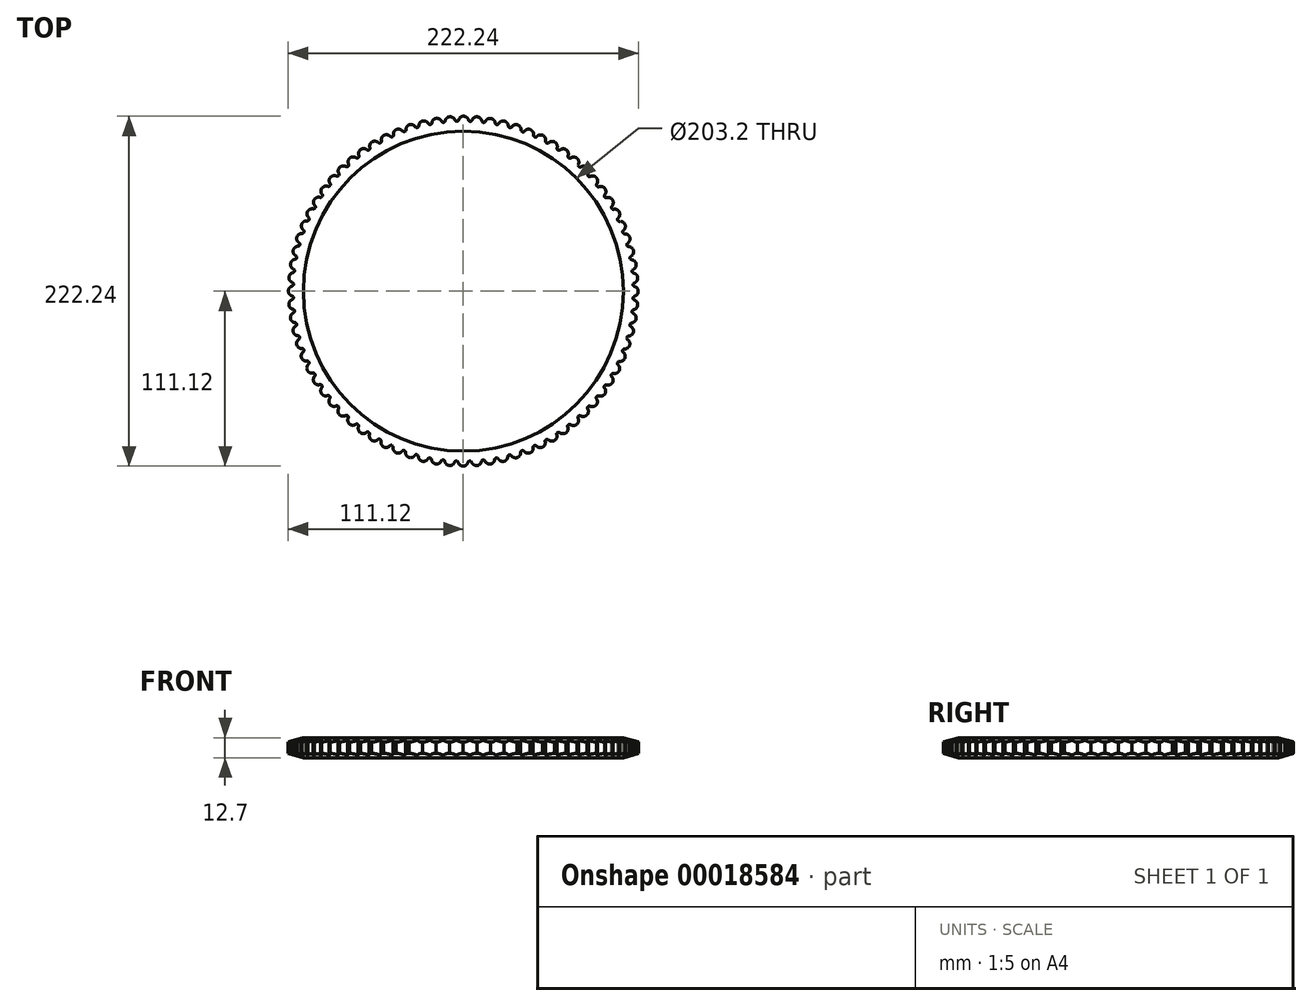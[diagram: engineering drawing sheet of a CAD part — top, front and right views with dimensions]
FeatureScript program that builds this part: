
annotation { "Feature Type Name" : "Feature", "Feature Type Description" : "" }
export const myFeature = defineFeature(function(context is Context, id is Id, definition is map)
    precondition{}
    {
        {
            var Q0;
            Q0=qCreatedBy(makeId("Top.planeOp"),FACE);
            var sketch = newSketch(context, id + "F0", { "sketchPlane" : qUnion([Q0])});
            skCircle(sketch, "E0", {"center": v(0, 0) * mm, "radius": 101.6 * mm});
            skCircle(sketch, "E1", {"center": v(0, 0) * mm, "radius": 111.13 * mm});
            skSolve(sketch);
        }
        {
            var Q0;
            Q0 = qSketchRegion(id + "F0", true);
            extrude(context, id + "F1", {"entities" : qUnion([Q0]), "depth" : 12.7 * mm});
        }
        {
            var Q0;
            Q0=makeQuery(id+"F1.opExtrude","CAP_FACE",FACE,{"disambiguationData":[OSD([sQuery(id+"F0.wireOp",EDGE,"E0"),sQuery(id+"F0.wireOp",EDGE,"E1")])],"isStart":false});
            var sketch = newSketch(context, id + "F2", { "sketchPlane" : qUnion([Q0])});
            skLineSegment(sketch, "E2", {"start": v(0, 0) * mm, "end": v(0, 111.13) * mm, "construction": true});
            skArc(sketch, "E3", {"start": v(3.3, 108.7) * mm, "mid": v(2.05, 110.45) * mm, "end": v(0, 111.13) * mm});
            skCircle(sketch, "E4", {"center": v(0, 0) * mm, "radius": 107.95 * mm, "construction": true});
            skArc(sketch, "E5", {"start": v(8.83, 110.77) * mm, "mid": v(6.85, 110.27) * mm, "end": v(5.59, 108.66) * mm});
            skArc(sketch, "E6", {"start": v(3.3, 108.7) * mm, "mid": v(4.43, 107.86) * mm, "end": v(5.59, 108.66) * mm});
            skLineSegment(sketch, "E7", {"start": v(8.58, 107.6) * mm, "end": v(8.83, 110.77) * mm, "construction": true});
            skArc(sketch, "E8.1.0", {"start": v(-5.24, 108.63) * mm, "mid": v(-6.62, 110.27) * mm, "end": v(-8.72, 110.78) * mm});
            skArc(sketch, "E8.1.1", {"start": v(0.12, 111.12) * mm, "mid": v(-1.82, 110.47) * mm, "end": v(-2.96, 108.77) * mm});
            skArc(sketch, "E8.1.2", {"start": v(-5.24, 108.63) * mm, "mid": v(-4.05, 107.87) * mm, "end": v(-2.96, 108.77) * mm});
            skArc(sketch, "E8.2.0", {"start": v(-13.74, 107.88) * mm, "mid": v(-15.26, 109.41) * mm, "end": v(-17.38, 109.76) * mm});
            skArc(sketch, "E8.2.1", {"start": v(-8.6, 110.8) * mm, "mid": v(-10.48, 109.98) * mm, "end": v(-11.48, 108.2) * mm});
            skArc(sketch, "E8.2.2", {"start": v(-13.74, 107.88) * mm, "mid": v(-12.5, 107.22) * mm, "end": v(-11.48, 108.2) * mm});
            skArc(sketch, "E8.3.0", {"start": v(-22.16, 106.47) * mm, "mid": v(-23.8, 107.88) * mm, "end": v(-25.94, 108.05) * mm});
            skArc(sketch, "E8.3.1", {"start": v(-17.27, 109.77) * mm, "mid": v(-19.08, 108.82) * mm, "end": v(-19.93, 106.97) * mm});
            skArc(sketch, "E8.3.2", {"start": v(-22.16, 106.47) * mm, "mid": v(-20.87, 105.91) * mm, "end": v(-19.93, 106.97) * mm});
            skArc(sketch, "E8.4.0", {"start": v(-30.45, 104.4) * mm, "mid": v(-32.18, 105.68) * mm, "end": v(-34.34, 105.69) * mm});
            skArc(sketch, "E8.4.1", {"start": v(-25.83, 108.08) * mm, "mid": v(-27.56, 107) * mm, "end": v(-28.26, 105.07) * mm});
            skArc(sketch, "E8.4.2", {"start": v(-30.45, 104.4) * mm, "mid": v(-29.12, 103.95) * mm, "end": v(-28.26, 105.07) * mm});
            skArc(sketch, "E8.5.0", {"start": v(-38.55, 101.7) * mm, "mid": v(-40.38, 102.83) * mm, "end": v(-42.53, 102.67) * mm});
            skArc(sketch, "E8.5.1", {"start": v(-34.23, 105.72) * mm, "mid": v(-35.87, 104.5) * mm, "end": v(-36.42, 102.53) * mm});
            skArc(sketch, "E8.5.2", {"start": v(-38.55, 101.7) * mm, "mid": v(-37.18, 101.34) * mm, "end": v(-36.42, 102.53) * mm});
            skArc(sketch, "E8.6.0", {"start": v(-46.4, 98.35) * mm, "mid": v(-48.32, 99.35) * mm, "end": v(-50.45, 99.01) * mm});
            skArc(sketch, "E8.6.1", {"start": v(-42.42, 102.71) * mm, "mid": v(-43.96, 101.36) * mm, "end": v(-44.35, 99.36) * mm});
            skArc(sketch, "E8.6.2", {"start": v(-46.4, 98.35) * mm, "mid": v(-45.02, 98.12) * mm, "end": v(-44.35, 99.36) * mm});
            skArc(sketch, "E8.7.0", {"start": v(-53.98, 94.4) * mm, "mid": v(-55.97, 95.25) * mm, "end": v(-58.06, 94.75) * mm});
            skArc(sketch, "E8.7.1", {"start": v(-50.35, 99.07) * mm, "mid": v(-51.77, 97.6) * mm, "end": v(-52.01, 95.57) * mm});
            skArc(sketch, "E8.7.2", {"start": v(-53.98, 94.4) * mm, "mid": v(-52.58, 94.28) * mm, "end": v(-52.01, 95.57) * mm});
            skArc(sketch, "E8.8.0", {"start": v(-61.22, 89.88) * mm, "mid": v(-63.27, 90.56) * mm, "end": v(-65.32, 89.9) * mm});
            skArc(sketch, "E8.8.1", {"start": v(-57.96, 94.81) * mm, "mid": v(-59.27, 93.24) * mm, "end": v(-59.35, 91.2) * mm});
            skArc(sketch, "E8.8.2", {"start": v(-61.22, 89.88) * mm, "mid": v(-59.81, 89.86) * mm, "end": v(-59.35, 91.2) * mm});
            skArc(sketch, "E8.9.0", {"start": v(-68.09, 84.8) * mm, "mid": v(-70.18, 85.32) * mm, "end": v(-72.17, 84.5) * mm});
            skArc(sketch, "E8.9.1", {"start": v(-65.22, 89.97) * mm, "mid": v(-66.4, 88.3) * mm, "end": v(-66.32, 86.26) * mm});
            skArc(sketch, "E8.9.2", {"start": v(-68.09, 84.8) * mm, "mid": v(-66.68, 84.9) * mm, "end": v(-66.32, 86.26) * mm});
            skArc(sketch, "E8.10.0", {"start": v(-74.53, 79.2) * mm, "mid": v(-76.65, 79.55) * mm, "end": v(-78.58, 78.58) * mm});
            skArc(sketch, "E8.10.1", {"start": v(-72.08, 84.58) * mm, "mid": v(-73.13, 82.82) * mm, "end": v(-72.89, 80.79) * mm});
            skArc(sketch, "E8.10.2", {"start": v(-74.53, 79.2) * mm, "mid": v(-73.13, 79.4) * mm, "end": v(-72.89, 80.79) * mm});
            skArc(sketch, "E8.11.0", {"start": v(-80.51, 73.1) * mm, "mid": v(-82.66, 73.3) * mm, "end": v(-84.5, 72.17) * mm});
            skArc(sketch, "E8.11.1", {"start": v(-78.5, 78.66) * mm, "mid": v(-79.4, 76.83) * mm, "end": v(-79, 74.82) * mm});
            skArc(sketch, "E8.11.2", {"start": v(-80.51, 73.1) * mm, "mid": v(-79.14, 73.42) * mm, "end": v(-79, 74.82) * mm});
            skArc(sketch, "E8.12.0", {"start": v(-86, 66.57) * mm, "mid": v(-88.16, 66.58) * mm, "end": v(-89.9, 65.32) * mm});
            skArc(sketch, "E8.12.1", {"start": v(-84.42, 72.26) * mm, "mid": v(-85.18, 70.36) * mm, "end": v(-84.63, 68.4) * mm});
            skArc(sketch, "E8.12.2", {"start": v(-86, 66.57) * mm, "mid": v(-84.66, 66.98) * mm, "end": v(-84.63, 68.4) * mm});
            skArc(sketch, "E8.13.0", {"start": v(-90.96, 59.61) * mm, "mid": v(-93.1, 59.46) * mm, "end": v(-94.75, 58.06) * mm});
            skArc(sketch, "E8.13.1", {"start": v(-89.83, 65.41) * mm, "mid": v(-90.44, 63.46) * mm, "end": v(-89.73, 61.54) * mm});
            skArc(sketch, "E8.13.2", {"start": v(-90.96, 59.61) * mm, "mid": v(-89.65, 60.13) * mm, "end": v(-89.73, 61.54) * mm});
            skArc(sketch, "E8.14.0", {"start": v(-95.36, 52.3) * mm, "mid": v(-97.49, 51.97) * mm, "end": v(-99.01, 50.45) * mm});
            skArc(sketch, "E8.14.1", {"start": v(-94.69, 58.16) * mm, "mid": v(-95.14, 56.17) * mm, "end": v(-94.28, 54.31) * mm});
            skArc(sketch, "E8.14.2", {"start": v(-95.36, 52.3) * mm, "mid": v(-94.1, 52.92) * mm, "end": v(-94.28, 54.31) * mm});
            skArc(sketch, "E8.15.0", {"start": v(-99.16, 44.65) * mm, "mid": v(-101.26, 44.16) * mm, "end": v(-102.67, 42.53) * mm});
            skArc(sketch, "E8.15.1", {"start": v(-98.96, 50.55) * mm, "mid": v(-99.25, 48.53) * mm, "end": v(-98.25, 46.75) * mm});
            skArc(sketch, "E8.15.2", {"start": v(-99.16, 44.65) * mm, "mid": v(-97.95, 45.37) * mm, "end": v(-98.25, 46.75) * mm});
            skArc(sketch, "E8.16.0", {"start": v(-102.36, 36.73) * mm, "mid": v(-104.42, 36.08) * mm, "end": v(-105.69, 34.34) * mm});
            skArc(sketch, "E8.16.1", {"start": v(-102.62, 42.63) * mm, "mid": v(-102.76, 40.6) * mm, "end": v(-101.62, 38.9) * mm});
            skArc(sketch, "E8.16.2", {"start": v(-102.36, 36.73) * mm, "mid": v(-101.21, 37.54) * mm, "end": v(-101.62, 38.9) * mm});
            skArc(sketch, "E8.17.0", {"start": v(-104.93, 28.59) * mm, "mid": v(-106.92, 27.78) * mm, "end": v(-108.05, 25.94) * mm});
            skArc(sketch, "E8.17.1", {"start": v(-105.65, 34.45) * mm, "mid": v(-105.62, 32.4) * mm, "end": v(-104.36, 30.8) * mm});
            skArc(sketch, "E8.17.2", {"start": v(-104.93, 28.59) * mm, "mid": v(-103.84, 29.49) * mm, "end": v(-104.36, 30.8) * mm});
            skArc(sketch, "E8.18.0", {"start": v(-106.85, 20.27) * mm, "mid": v(-108.77, 19.3) * mm, "end": v(-109.76, 17.38) * mm});
            skArc(sketch, "E8.18.1", {"start": v(-108.03, 26.05) * mm, "mid": v(-107.84, 24.02) * mm, "end": v(-106.45, 22.52) * mm});
            skArc(sketch, "E8.18.2", {"start": v(-106.85, 20.27) * mm, "mid": v(-105.84, 21.25) * mm, "end": v(-106.45, 22.52) * mm});
            skArc(sketch, "E8.19.0", {"start": v(-108.1, 11.82) * mm, "mid": v(-109.95, 10.7) * mm, "end": v(-110.78, 8.72) * mm});
            skArc(sketch, "E8.19.1", {"start": v(-109.74, 17.5) * mm, "mid": v(-109.4, 15.48) * mm, "end": v(-107.9, 14.1) * mm});
            skArc(sketch, "E8.19.2", {"start": v(-108.1, 11.82) * mm, "mid": v(-107.18, 12.88) * mm, "end": v(-107.9, 14.1) * mm});
            skArc(sketch, "E8.20.0", {"start": v(-108.7, 3.3) * mm, "mid": v(-110.45, 2.05) * mm, "end": v(-111.13, 0) * mm});
            skArc(sketch, "E8.20.1", {"start": v(-110.77, 8.83) * mm, "mid": v(-110.27, 6.85) * mm, "end": v(-108.66, 5.59) * mm});
            skArc(sketch, "E8.20.2", {"start": v(-108.7, 3.3) * mm, "mid": v(-107.86, 4.43) * mm, "end": v(-108.66, 5.59) * mm});
            skArc(sketch, "E8.21.0", {"start": v(-108.63, -5.24) * mm, "mid": v(-110.27, -6.62) * mm, "end": v(-110.78, -8.72) * mm});
            skArc(sketch, "E8.21.1", {"start": v(-111.12, 0.12) * mm, "mid": v(-110.47, -1.82) * mm, "end": v(-108.77, -2.96) * mm});
            skArc(sketch, "E8.21.2", {"start": v(-108.63, -5.24) * mm, "mid": v(-107.87, -4.05) * mm, "end": v(-108.77, -2.96) * mm});
            skArc(sketch, "E8.22.0", {"start": v(-107.88, -13.74) * mm, "mid": v(-109.41, -15.26) * mm, "end": v(-109.76, -17.38) * mm});
            skArc(sketch, "E8.22.1", {"start": v(-110.8, -8.6) * mm, "mid": v(-109.98, -10.48) * mm, "end": v(-108.2, -11.48) * mm});
            skArc(sketch, "E8.22.2", {"start": v(-107.88, -13.74) * mm, "mid": v(-107.22, -12.5) * mm, "end": v(-108.2, -11.48) * mm});
            skArc(sketch, "E8.23.0", {"start": v(-106.47, -22.16) * mm, "mid": v(-107.88, -23.8) * mm, "end": v(-108.05, -25.94) * mm});
            skArc(sketch, "E8.23.1", {"start": v(-109.77, -17.27) * mm, "mid": v(-108.82, -19.08) * mm, "end": v(-106.97, -19.93) * mm});
            skArc(sketch, "E8.23.2", {"start": v(-106.47, -22.16) * mm, "mid": v(-105.91, -20.87) * mm, "end": v(-106.97, -19.93) * mm});
            skArc(sketch, "E8.24.0", {"start": v(-104.4, -30.45) * mm, "mid": v(-105.68, -32.18) * mm, "end": v(-105.69, -34.34) * mm});
            skArc(sketch, "E8.24.1", {"start": v(-108.08, -25.83) * mm, "mid": v(-107, -27.56) * mm, "end": v(-105.07, -28.26) * mm});
            skArc(sketch, "E8.24.2", {"start": v(-104.4, -30.45) * mm, "mid": v(-103.95, -29.12) * mm, "end": v(-105.07, -28.26) * mm});
            skArc(sketch, "E8.25.0", {"start": v(-101.7, -38.55) * mm, "mid": v(-102.83, -40.38) * mm, "end": v(-102.67, -42.53) * mm});
            skArc(sketch, "E8.25.1", {"start": v(-105.72, -34.23) * mm, "mid": v(-104.5, -35.87) * mm, "end": v(-102.53, -36.42) * mm});
            skArc(sketch, "E8.25.2", {"start": v(-101.7, -38.55) * mm, "mid": v(-101.34, -37.18) * mm, "end": v(-102.53, -36.42) * mm});
            skArc(sketch, "E8.26.0", {"start": v(-98.35, -46.4) * mm, "mid": v(-99.35, -48.32) * mm, "end": v(-99.01, -50.45) * mm});
            skArc(sketch, "E8.26.1", {"start": v(-102.71, -42.42) * mm, "mid": v(-101.36, -43.96) * mm, "end": v(-99.36, -44.35) * mm});
            skArc(sketch, "E8.26.2", {"start": v(-98.35, -46.4) * mm, "mid": v(-98.12, -45.02) * mm, "end": v(-99.36, -44.35) * mm});
            skArc(sketch, "E8.27.0", {"start": v(-94.4, -53.98) * mm, "mid": v(-95.25, -55.97) * mm, "end": v(-94.75, -58.06) * mm});
            skArc(sketch, "E8.27.1", {"start": v(-99.07, -50.35) * mm, "mid": v(-97.6, -51.77) * mm, "end": v(-95.57, -52.01) * mm});
            skArc(sketch, "E8.27.2", {"start": v(-94.4, -53.98) * mm, "mid": v(-94.28, -52.58) * mm, "end": v(-95.57, -52.01) * mm});
            skArc(sketch, "E8.28.0", {"start": v(-89.88, -61.22) * mm, "mid": v(-90.56, -63.27) * mm, "end": v(-89.9, -65.32) * mm});
            skArc(sketch, "E8.28.1", {"start": v(-94.81, -57.96) * mm, "mid": v(-93.24, -59.27) * mm, "end": v(-91.2, -59.35) * mm});
            skArc(sketch, "E8.28.2", {"start": v(-89.88, -61.22) * mm, "mid": v(-89.86, -59.81) * mm, "end": v(-91.2, -59.35) * mm});
            skArc(sketch, "E8.29.0", {"start": v(-84.8, -68.09) * mm, "mid": v(-85.32, -70.18) * mm, "end": v(-84.5, -72.17) * mm});
            skArc(sketch, "E8.29.1", {"start": v(-89.97, -65.22) * mm, "mid": v(-88.3, -66.4) * mm, "end": v(-86.26, -66.32) * mm});
            skArc(sketch, "E8.29.2", {"start": v(-84.8, -68.09) * mm, "mid": v(-84.9, -66.68) * mm, "end": v(-86.26, -66.32) * mm});
            skArc(sketch, "E8.30.0", {"start": v(-79.2, -74.53) * mm, "mid": v(-79.55, -76.65) * mm, "end": v(-78.58, -78.58) * mm});
            skArc(sketch, "E8.30.1", {"start": v(-84.58, -72.08) * mm, "mid": v(-82.82, -73.13) * mm, "end": v(-80.79, -72.89) * mm});
            skArc(sketch, "E8.30.2", {"start": v(-79.2, -74.53) * mm, "mid": v(-79.4, -73.13) * mm, "end": v(-80.79, -72.89) * mm});
            skArc(sketch, "E8.31.0", {"start": v(-73.1, -80.51) * mm, "mid": v(-73.3, -82.66) * mm, "end": v(-72.17, -84.5) * mm});
            skArc(sketch, "E8.31.1", {"start": v(-78.66, -78.5) * mm, "mid": v(-76.83, -79.4) * mm, "end": v(-74.82, -79) * mm});
            skArc(sketch, "E8.31.2", {"start": v(-73.1, -80.51) * mm, "mid": v(-73.42, -79.14) * mm, "end": v(-74.82, -79) * mm});
            skArc(sketch, "E8.32.0", {"start": v(-66.57, -86) * mm, "mid": v(-66.58, -88.16) * mm, "end": v(-65.32, -89.9) * mm});
            skArc(sketch, "E8.32.1", {"start": v(-72.26, -84.42) * mm, "mid": v(-70.36, -85.18) * mm, "end": v(-68.4, -84.63) * mm});
            skArc(sketch, "E8.32.2", {"start": v(-66.57, -86) * mm, "mid": v(-66.98, -84.66) * mm, "end": v(-68.4, -84.63) * mm});
            skArc(sketch, "E8.33.0", {"start": v(-59.61, -90.96) * mm, "mid": v(-59.46, -93.1) * mm, "end": v(-58.06, -94.75) * mm});
            skArc(sketch, "E8.33.1", {"start": v(-65.41, -89.83) * mm, "mid": v(-63.46, -90.44) * mm, "end": v(-61.54, -89.73) * mm});
            skArc(sketch, "E8.33.2", {"start": v(-59.61, -90.96) * mm, "mid": v(-60.13, -89.65) * mm, "end": v(-61.54, -89.73) * mm});
            skArc(sketch, "E8.34.0", {"start": v(-52.3, -95.36) * mm, "mid": v(-51.97, -97.49) * mm, "end": v(-50.45, -99.01) * mm});
            skArc(sketch, "E8.34.1", {"start": v(-58.16, -94.69) * mm, "mid": v(-56.17, -95.14) * mm, "end": v(-54.31, -94.28) * mm});
            skArc(sketch, "E8.34.2", {"start": v(-52.3, -95.36) * mm, "mid": v(-52.92, -94.1) * mm, "end": v(-54.31, -94.28) * mm});
            skArc(sketch, "E8.35.0", {"start": v(-44.65, -99.16) * mm, "mid": v(-44.16, -101.26) * mm, "end": v(-42.53, -102.67) * mm});
            skArc(sketch, "E8.35.1", {"start": v(-50.55, -98.96) * mm, "mid": v(-48.53, -99.25) * mm, "end": v(-46.75, -98.25) * mm});
            skArc(sketch, "E8.35.2", {"start": v(-44.65, -99.16) * mm, "mid": v(-45.37, -97.95) * mm, "end": v(-46.75, -98.25) * mm});
            skArc(sketch, "E8.36.0", {"start": v(-36.73, -102.36) * mm, "mid": v(-36.08, -104.42) * mm, "end": v(-34.34, -105.69) * mm});
            skArc(sketch, "E8.36.1", {"start": v(-42.63, -102.62) * mm, "mid": v(-40.6, -102.76) * mm, "end": v(-38.9, -101.62) * mm});
            skArc(sketch, "E8.36.2", {"start": v(-36.73, -102.36) * mm, "mid": v(-37.54, -101.21) * mm, "end": v(-38.9, -101.62) * mm});
            skArc(sketch, "E8.37.0", {"start": v(-28.59, -104.93) * mm, "mid": v(-27.78, -106.92) * mm, "end": v(-25.94, -108.05) * mm});
            skArc(sketch, "E8.37.1", {"start": v(-34.45, -105.65) * mm, "mid": v(-32.4, -105.62) * mm, "end": v(-30.8, -104.36) * mm});
            skArc(sketch, "E8.37.2", {"start": v(-28.59, -104.93) * mm, "mid": v(-29.49, -103.84) * mm, "end": v(-30.8, -104.36) * mm});
            skArc(sketch, "E8.38.0", {"start": v(-20.27, -106.85) * mm, "mid": v(-19.3, -108.77) * mm, "end": v(-17.38, -109.76) * mm});
            skArc(sketch, "E8.38.1", {"start": v(-26.05, -108.03) * mm, "mid": v(-24.02, -107.84) * mm, "end": v(-22.52, -106.45) * mm});
            skArc(sketch, "E8.38.2", {"start": v(-20.27, -106.85) * mm, "mid": v(-21.25, -105.84) * mm, "end": v(-22.52, -106.45) * mm});
            skArc(sketch, "E8.39.0", {"start": v(-11.82, -108.1) * mm, "mid": v(-10.7, -109.95) * mm, "end": v(-8.72, -110.78) * mm});
            skArc(sketch, "E8.39.1", {"start": v(-17.5, -109.74) * mm, "mid": v(-15.48, -109.4) * mm, "end": v(-14.1, -107.9) * mm});
            skArc(sketch, "E8.39.2", {"start": v(-11.82, -108.1) * mm, "mid": v(-12.88, -107.18) * mm, "end": v(-14.1, -107.9) * mm});
            skArc(sketch, "E8.40.0", {"start": v(-3.3, -108.7) * mm, "mid": v(-2.05, -110.45) * mm, "end": v(0, -111.13) * mm});
            skArc(sketch, "E8.40.1", {"start": v(-8.83, -110.77) * mm, "mid": v(-6.85, -110.27) * mm, "end": v(-5.59, -108.66) * mm});
            skArc(sketch, "E8.40.2", {"start": v(-3.3, -108.7) * mm, "mid": v(-4.43, -107.86) * mm, "end": v(-5.59, -108.66) * mm});
            skArc(sketch, "E8.41.0", {"start": v(5.24, -108.63) * mm, "mid": v(6.62, -110.27) * mm, "end": v(8.72, -110.78) * mm});
            skArc(sketch, "E8.41.1", {"start": v(-0.12, -111.12) * mm, "mid": v(1.82, -110.47) * mm, "end": v(2.96, -108.77) * mm});
            skArc(sketch, "E8.41.2", {"start": v(5.24, -108.63) * mm, "mid": v(4.05, -107.87) * mm, "end": v(2.96, -108.77) * mm});
            skArc(sketch, "E8.42.0", {"start": v(13.74, -107.88) * mm, "mid": v(15.26, -109.41) * mm, "end": v(17.38, -109.76) * mm});
            skArc(sketch, "E8.42.1", {"start": v(8.6, -110.8) * mm, "mid": v(10.48, -109.98) * mm, "end": v(11.48, -108.2) * mm});
            skArc(sketch, "E8.42.2", {"start": v(13.74, -107.88) * mm, "mid": v(12.5, -107.22) * mm, "end": v(11.48, -108.2) * mm});
            skArc(sketch, "E8.43.0", {"start": v(22.16, -106.47) * mm, "mid": v(23.8, -107.88) * mm, "end": v(25.94, -108.05) * mm});
            skArc(sketch, "E8.43.1", {"start": v(17.27, -109.77) * mm, "mid": v(19.08, -108.82) * mm, "end": v(19.93, -106.97) * mm});
            skArc(sketch, "E8.43.2", {"start": v(22.16, -106.47) * mm, "mid": v(20.87, -105.91) * mm, "end": v(19.93, -106.97) * mm});
            skArc(sketch, "E8.44.0", {"start": v(30.45, -104.4) * mm, "mid": v(32.18, -105.68) * mm, "end": v(34.34, -105.69) * mm});
            skArc(sketch, "E8.44.1", {"start": v(25.83, -108.08) * mm, "mid": v(27.56, -107) * mm, "end": v(28.26, -105.07) * mm});
            skArc(sketch, "E8.44.2", {"start": v(30.45, -104.4) * mm, "mid": v(29.12, -103.95) * mm, "end": v(28.26, -105.07) * mm});
            skArc(sketch, "E8.45.0", {"start": v(38.55, -101.7) * mm, "mid": v(40.38, -102.83) * mm, "end": v(42.53, -102.67) * mm});
            skArc(sketch, "E8.45.1", {"start": v(34.23, -105.72) * mm, "mid": v(35.87, -104.5) * mm, "end": v(36.42, -102.53) * mm});
            skArc(sketch, "E8.45.2", {"start": v(38.55, -101.7) * mm, "mid": v(37.18, -101.34) * mm, "end": v(36.42, -102.53) * mm});
            skArc(sketch, "E8.46.0", {"start": v(46.4, -98.35) * mm, "mid": v(48.32, -99.35) * mm, "end": v(50.45, -99.01) * mm});
            skArc(sketch, "E8.46.1", {"start": v(42.42, -102.71) * mm, "mid": v(43.96, -101.36) * mm, "end": v(44.35, -99.36) * mm});
            skArc(sketch, "E8.46.2", {"start": v(46.4, -98.35) * mm, "mid": v(45.02, -98.12) * mm, "end": v(44.35, -99.36) * mm});
            skArc(sketch, "E8.47.0", {"start": v(53.98, -94.4) * mm, "mid": v(55.97, -95.25) * mm, "end": v(58.06, -94.75) * mm});
            skArc(sketch, "E8.47.1", {"start": v(50.35, -99.07) * mm, "mid": v(51.77, -97.6) * mm, "end": v(52.01, -95.57) * mm});
            skArc(sketch, "E8.47.2", {"start": v(53.98, -94.4) * mm, "mid": v(52.58, -94.28) * mm, "end": v(52.01, -95.57) * mm});
            skArc(sketch, "E8.48.0", {"start": v(61.22, -89.88) * mm, "mid": v(63.27, -90.56) * mm, "end": v(65.32, -89.9) * mm});
            skArc(sketch, "E8.48.1", {"start": v(57.96, -94.81) * mm, "mid": v(59.27, -93.24) * mm, "end": v(59.35, -91.2) * mm});
            skArc(sketch, "E8.48.2", {"start": v(61.22, -89.88) * mm, "mid": v(59.81, -89.86) * mm, "end": v(59.35, -91.2) * mm});
            skArc(sketch, "E8.49.0", {"start": v(68.09, -84.8) * mm, "mid": v(70.18, -85.32) * mm, "end": v(72.17, -84.5) * mm});
            skArc(sketch, "E8.49.1", {"start": v(65.22, -89.97) * mm, "mid": v(66.4, -88.3) * mm, "end": v(66.32, -86.26) * mm});
            skArc(sketch, "E8.49.2", {"start": v(68.09, -84.8) * mm, "mid": v(66.68, -84.9) * mm, "end": v(66.32, -86.26) * mm});
            skArc(sketch, "E8.50.0", {"start": v(74.53, -79.2) * mm, "mid": v(76.65, -79.55) * mm, "end": v(78.58, -78.58) * mm});
            skArc(sketch, "E8.50.1", {"start": v(72.08, -84.58) * mm, "mid": v(73.13, -82.82) * mm, "end": v(72.89, -80.79) * mm});
            skArc(sketch, "E8.50.2", {"start": v(74.53, -79.2) * mm, "mid": v(73.13, -79.4) * mm, "end": v(72.89, -80.79) * mm});
            skArc(sketch, "E8.51.0", {"start": v(80.51, -73.1) * mm, "mid": v(82.66, -73.3) * mm, "end": v(84.5, -72.17) * mm});
            skArc(sketch, "E8.51.1", {"start": v(78.5, -78.66) * mm, "mid": v(79.4, -76.83) * mm, "end": v(79, -74.82) * mm});
            skArc(sketch, "E8.51.2", {"start": v(80.51, -73.1) * mm, "mid": v(79.14, -73.42) * mm, "end": v(79, -74.82) * mm});
            skArc(sketch, "E8.52.0", {"start": v(86, -66.57) * mm, "mid": v(88.16, -66.58) * mm, "end": v(89.9, -65.32) * mm});
            skArc(sketch, "E8.52.1", {"start": v(84.42, -72.26) * mm, "mid": v(85.18, -70.36) * mm, "end": v(84.63, -68.4) * mm});
            skArc(sketch, "E8.52.2", {"start": v(86, -66.57) * mm, "mid": v(84.66, -66.98) * mm, "end": v(84.63, -68.4) * mm});
            skArc(sketch, "E8.53.0", {"start": v(90.96, -59.61) * mm, "mid": v(93.1, -59.46) * mm, "end": v(94.75, -58.06) * mm});
            skArc(sketch, "E8.53.1", {"start": v(89.83, -65.41) * mm, "mid": v(90.44, -63.46) * mm, "end": v(89.73, -61.54) * mm});
            skArc(sketch, "E8.53.2", {"start": v(90.96, -59.61) * mm, "mid": v(89.65, -60.13) * mm, "end": v(89.73, -61.54) * mm});
            skArc(sketch, "E8.54.0", {"start": v(95.36, -52.3) * mm, "mid": v(97.49, -51.97) * mm, "end": v(99.01, -50.45) * mm});
            skArc(sketch, "E8.54.1", {"start": v(94.69, -58.16) * mm, "mid": v(95.14, -56.17) * mm, "end": v(94.28, -54.31) * mm});
            skArc(sketch, "E8.54.2", {"start": v(95.36, -52.3) * mm, "mid": v(94.1, -52.92) * mm, "end": v(94.28, -54.31) * mm});
            skArc(sketch, "E8.55.0", {"start": v(99.16, -44.65) * mm, "mid": v(101.26, -44.16) * mm, "end": v(102.67, -42.53) * mm});
            skArc(sketch, "E8.55.1", {"start": v(98.96, -50.55) * mm, "mid": v(99.25, -48.53) * mm, "end": v(98.25, -46.75) * mm});
            skArc(sketch, "E8.55.2", {"start": v(99.16, -44.65) * mm, "mid": v(97.95, -45.37) * mm, "end": v(98.25, -46.75) * mm});
            skArc(sketch, "E8.56.0", {"start": v(102.36, -36.73) * mm, "mid": v(104.42, -36.08) * mm, "end": v(105.69, -34.34) * mm});
            skArc(sketch, "E8.56.1", {"start": v(102.62, -42.63) * mm, "mid": v(102.76, -40.6) * mm, "end": v(101.62, -38.9) * mm});
            skArc(sketch, "E8.56.2", {"start": v(102.36, -36.73) * mm, "mid": v(101.21, -37.54) * mm, "end": v(101.62, -38.9) * mm});
            skArc(sketch, "E8.57.0", {"start": v(104.93, -28.59) * mm, "mid": v(106.92, -27.78) * mm, "end": v(108.05, -25.94) * mm});
            skArc(sketch, "E8.57.1", {"start": v(105.65, -34.45) * mm, "mid": v(105.62, -32.4) * mm, "end": v(104.36, -30.8) * mm});
            skArc(sketch, "E8.57.2", {"start": v(104.93, -28.59) * mm, "mid": v(103.84, -29.49) * mm, "end": v(104.36, -30.8) * mm});
            skArc(sketch, "E8.58.0", {"start": v(106.85, -20.27) * mm, "mid": v(108.77, -19.3) * mm, "end": v(109.76, -17.38) * mm});
            skArc(sketch, "E8.58.1", {"start": v(108.03, -26.05) * mm, "mid": v(107.84, -24.02) * mm, "end": v(106.45, -22.52) * mm});
            skArc(sketch, "E8.58.2", {"start": v(106.85, -20.27) * mm, "mid": v(105.84, -21.25) * mm, "end": v(106.45, -22.52) * mm});
            skArc(sketch, "E8.59.0", {"start": v(108.1, -11.82) * mm, "mid": v(109.95, -10.7) * mm, "end": v(110.78, -8.72) * mm});
            skArc(sketch, "E8.59.1", {"start": v(109.74, -17.5) * mm, "mid": v(109.4, -15.48) * mm, "end": v(107.9, -14.1) * mm});
            skArc(sketch, "E8.59.2", {"start": v(108.1, -11.82) * mm, "mid": v(107.18, -12.88) * mm, "end": v(107.9, -14.1) * mm});
            skArc(sketch, "E8.60.0", {"start": v(108.7, -3.3) * mm, "mid": v(110.45, -2.05) * mm, "end": v(111.13, 0) * mm});
            skArc(sketch, "E8.60.1", {"start": v(110.77, -8.83) * mm, "mid": v(110.27, -6.85) * mm, "end": v(108.66, -5.59) * mm});
            skArc(sketch, "E8.60.2", {"start": v(108.7, -3.3) * mm, "mid": v(107.86, -4.43) * mm, "end": v(108.66, -5.59) * mm});
            skArc(sketch, "E8.61.0", {"start": v(108.63, 5.24) * mm, "mid": v(110.27, 6.62) * mm, "end": v(110.78, 8.72) * mm});
            skArc(sketch, "E8.61.1", {"start": v(111.12, -0.12) * mm, "mid": v(110.47, 1.82) * mm, "end": v(108.77, 2.96) * mm});
            skArc(sketch, "E8.61.2", {"start": v(108.63, 5.24) * mm, "mid": v(107.87, 4.05) * mm, "end": v(108.77, 2.96) * mm});
            skArc(sketch, "E8.62.0", {"start": v(107.88, 13.74) * mm, "mid": v(109.41, 15.26) * mm, "end": v(109.76, 17.38) * mm});
            skArc(sketch, "E8.62.1", {"start": v(110.8, 8.6) * mm, "mid": v(109.98, 10.48) * mm, "end": v(108.2, 11.48) * mm});
            skArc(sketch, "E8.62.2", {"start": v(107.88, 13.74) * mm, "mid": v(107.22, 12.5) * mm, "end": v(108.2, 11.48) * mm});
            skArc(sketch, "E8.63.0", {"start": v(106.47, 22.16) * mm, "mid": v(107.88, 23.8) * mm, "end": v(108.05, 25.94) * mm});
            skArc(sketch, "E8.63.1", {"start": v(109.77, 17.27) * mm, "mid": v(108.82, 19.08) * mm, "end": v(106.97, 19.93) * mm});
            skArc(sketch, "E8.63.2", {"start": v(106.47, 22.16) * mm, "mid": v(105.91, 20.87) * mm, "end": v(106.97, 19.93) * mm});
            skArc(sketch, "E8.64.0", {"start": v(104.4, 30.45) * mm, "mid": v(105.68, 32.18) * mm, "end": v(105.69, 34.34) * mm});
            skArc(sketch, "E8.64.1", {"start": v(108.08, 25.83) * mm, "mid": v(107, 27.56) * mm, "end": v(105.07, 28.26) * mm});
            skArc(sketch, "E8.64.2", {"start": v(104.4, 30.45) * mm, "mid": v(103.95, 29.12) * mm, "end": v(105.07, 28.26) * mm});
            skArc(sketch, "E8.65.0", {"start": v(101.7, 38.55) * mm, "mid": v(102.83, 40.38) * mm, "end": v(102.67, 42.53) * mm});
            skArc(sketch, "E8.65.1", {"start": v(105.72, 34.23) * mm, "mid": v(104.5, 35.87) * mm, "end": v(102.53, 36.42) * mm});
            skArc(sketch, "E8.65.2", {"start": v(101.7, 38.55) * mm, "mid": v(101.34, 37.18) * mm, "end": v(102.53, 36.42) * mm});
            skArc(sketch, "E8.66.0", {"start": v(98.35, 46.4) * mm, "mid": v(99.35, 48.32) * mm, "end": v(99.01, 50.45) * mm});
            skArc(sketch, "E8.66.1", {"start": v(102.71, 42.42) * mm, "mid": v(101.36, 43.96) * mm, "end": v(99.36, 44.35) * mm});
            skArc(sketch, "E8.66.2", {"start": v(98.35, 46.4) * mm, "mid": v(98.12, 45.02) * mm, "end": v(99.36, 44.35) * mm});
            skArc(sketch, "E8.67.0", {"start": v(94.4, 53.98) * mm, "mid": v(95.25, 55.97) * mm, "end": v(94.75, 58.06) * mm});
            skArc(sketch, "E8.67.1", {"start": v(99.07, 50.35) * mm, "mid": v(97.6, 51.77) * mm, "end": v(95.57, 52.01) * mm});
            skArc(sketch, "E8.67.2", {"start": v(94.4, 53.98) * mm, "mid": v(94.28, 52.58) * mm, "end": v(95.57, 52.01) * mm});
            skArc(sketch, "E8.68.0", {"start": v(89.88, 61.22) * mm, "mid": v(90.56, 63.27) * mm, "end": v(89.9, 65.32) * mm});
            skArc(sketch, "E8.68.1", {"start": v(94.81, 57.96) * mm, "mid": v(93.24, 59.27) * mm, "end": v(91.2, 59.35) * mm});
            skArc(sketch, "E8.68.2", {"start": v(89.88, 61.22) * mm, "mid": v(89.86, 59.81) * mm, "end": v(91.2, 59.35) * mm});
            skArc(sketch, "E8.69.0", {"start": v(84.8, 68.09) * mm, "mid": v(85.32, 70.18) * mm, "end": v(84.5, 72.17) * mm});
            skArc(sketch, "E8.69.1", {"start": v(89.97, 65.22) * mm, "mid": v(88.3, 66.4) * mm, "end": v(86.26, 66.32) * mm});
            skArc(sketch, "E8.69.2", {"start": v(84.8, 68.09) * mm, "mid": v(84.9, 66.68) * mm, "end": v(86.26, 66.32) * mm});
            skArc(sketch, "E8.70.0", {"start": v(79.2, 74.53) * mm, "mid": v(79.55, 76.65) * mm, "end": v(78.58, 78.58) * mm});
            skArc(sketch, "E8.70.1", {"start": v(84.58, 72.08) * mm, "mid": v(82.82, 73.13) * mm, "end": v(80.79, 72.89) * mm});
            skArc(sketch, "E8.70.2", {"start": v(79.2, 74.53) * mm, "mid": v(79.4, 73.13) * mm, "end": v(80.79, 72.89) * mm});
            skArc(sketch, "E8.71.0", {"start": v(73.1, 80.51) * mm, "mid": v(73.3, 82.66) * mm, "end": v(72.17, 84.5) * mm});
            skArc(sketch, "E8.71.1", {"start": v(78.66, 78.5) * mm, "mid": v(76.83, 79.4) * mm, "end": v(74.82, 79) * mm});
            skArc(sketch, "E8.71.2", {"start": v(73.1, 80.51) * mm, "mid": v(73.42, 79.14) * mm, "end": v(74.82, 79) * mm});
            skArc(sketch, "E8.72.0", {"start": v(66.57, 86) * mm, "mid": v(66.58, 88.16) * mm, "end": v(65.32, 89.9) * mm});
            skArc(sketch, "E8.72.1", {"start": v(72.26, 84.42) * mm, "mid": v(70.36, 85.18) * mm, "end": v(68.4, 84.63) * mm});
            skArc(sketch, "E8.72.2", {"start": v(66.57, 86) * mm, "mid": v(66.98, 84.66) * mm, "end": v(68.4, 84.63) * mm});
            skArc(sketch, "E8.73.0", {"start": v(59.61, 90.96) * mm, "mid": v(59.46, 93.1) * mm, "end": v(58.06, 94.75) * mm});
            skArc(sketch, "E8.73.1", {"start": v(65.41, 89.83) * mm, "mid": v(63.46, 90.44) * mm, "end": v(61.54, 89.73) * mm});
            skArc(sketch, "E8.73.2", {"start": v(59.61, 90.96) * mm, "mid": v(60.13, 89.65) * mm, "end": v(61.54, 89.73) * mm});
            skArc(sketch, "E8.74.0", {"start": v(52.3, 95.36) * mm, "mid": v(51.97, 97.49) * mm, "end": v(50.45, 99.01) * mm});
            skArc(sketch, "E8.74.1", {"start": v(58.16, 94.69) * mm, "mid": v(56.17, 95.14) * mm, "end": v(54.31, 94.28) * mm});
            skArc(sketch, "E8.74.2", {"start": v(52.3, 95.36) * mm, "mid": v(52.92, 94.1) * mm, "end": v(54.31, 94.28) * mm});
            skArc(sketch, "E8.75.0", {"start": v(44.65, 99.16) * mm, "mid": v(44.16, 101.26) * mm, "end": v(42.53, 102.67) * mm});
            skArc(sketch, "E8.75.1", {"start": v(50.55, 98.96) * mm, "mid": v(48.53, 99.25) * mm, "end": v(46.75, 98.25) * mm});
            skArc(sketch, "E8.75.2", {"start": v(44.65, 99.16) * mm, "mid": v(45.37, 97.95) * mm, "end": v(46.75, 98.25) * mm});
            skArc(sketch, "E8.76.0", {"start": v(36.73, 102.36) * mm, "mid": v(36.08, 104.42) * mm, "end": v(34.34, 105.69) * mm});
            skArc(sketch, "E8.76.1", {"start": v(42.63, 102.62) * mm, "mid": v(40.6, 102.76) * mm, "end": v(38.9, 101.62) * mm});
            skArc(sketch, "E8.76.2", {"start": v(36.73, 102.36) * mm, "mid": v(37.54, 101.21) * mm, "end": v(38.9, 101.62) * mm});
            skArc(sketch, "E8.77.0", {"start": v(28.59, 104.93) * mm, "mid": v(27.78, 106.92) * mm, "end": v(25.94, 108.05) * mm});
            skArc(sketch, "E8.77.1", {"start": v(34.45, 105.65) * mm, "mid": v(32.4, 105.62) * mm, "end": v(30.8, 104.36) * mm});
            skArc(sketch, "E8.77.2", {"start": v(28.59, 104.93) * mm, "mid": v(29.49, 103.84) * mm, "end": v(30.8, 104.36) * mm});
            skArc(sketch, "E8.78.0", {"start": v(20.27, 106.85) * mm, "mid": v(19.3, 108.77) * mm, "end": v(17.38, 109.76) * mm});
            skArc(sketch, "E8.78.1", {"start": v(26.05, 108.03) * mm, "mid": v(24.02, 107.84) * mm, "end": v(22.52, 106.45) * mm});
            skArc(sketch, "E8.78.2", {"start": v(20.27, 106.85) * mm, "mid": v(21.25, 105.84) * mm, "end": v(22.52, 106.45) * mm});
            skArc(sketch, "E8.79.0", {"start": v(11.82, 108.1) * mm, "mid": v(10.7, 109.95) * mm, "end": v(8.72, 110.78) * mm});
            skArc(sketch, "E8.79.1", {"start": v(17.5, 109.74) * mm, "mid": v(15.48, 109.4) * mm, "end": v(14.1, 107.9) * mm});
            skArc(sketch, "E8.79.2", {"start": v(11.82, 108.1) * mm, "mid": v(12.88, 107.18) * mm, "end": v(14.1, 107.9) * mm});
            skCircle(sketch, "E9", {"center": v(0, 0) * mm, "radius": 129.3 * mm});
            skSolve(sketch);
        }
        {
            var Q0;
            Q0 = qSketchRegion(id + "F2", true);
            extrude(context, id + "F3", {"entities" : qUnion([Q0]), "operationType" : NewBodyOperationType.REMOVE, "oppositeDirection" : true, "depth" : 25.4 * mm});
        }
        {
            var Q0;
            Q0=qCreatedBy(makeId("Top.planeOp"),FACE);
            var sketch = newSketch(context, id + "F4", { "sketchPlane" : qUnion([Q0])});
            skCircle(sketch, "E10", {"center": v(0, 0) * mm, "radius": 106.71 * mm});
            skSolve(sketch);
        }
        {
            var Q0;
            Q0 = qSketchRegion(id + "F4", true);
            extrude(context, id + "F5", {"entities" : qUnion([Q0]), "depth" : 19.05 * mm, "hasSecondDirection" : true, "secondDirectionOppositeDirection" : true, "secondDirectionDepth" : 6.35 * mm});
        }
        {
            var Q0;
            Q0=makeQuery(id+"F5.opExtrude","CAP_EDGE",EDGE,{"disambiguationData":[OSD([sQuery(id+"F4.wireOp",EDGE,"E10")])],"isStart":false});
            var Q1;
            Q1=makeQuery(id+"F5.opExtrude","CAP_EDGE",EDGE,{"disambiguationData":[OSD([sQuery(id+"F4.wireOp",EDGE,"E10")])],"isStart":true});
            fillet(context, id + "F6", {"entities" : qUnion([Q0, Q1]), "radius" : 6.35 * mm, "tangentPropagation" : true, "allowEdgeOverflow" : false});
        }
        {
            var Q0;
            Q0=makeQuery(id+"F5.opExtrude","CAP_FACE",FACE,{"disambiguationData":[OSD([sQuery(id+"F4.wireOp",EDGE,"E10")])],"isStart":false});
            var sketch = newSketch(context, id + "F7", { "sketchPlane" : qUnion([Q0])});
            skArc(sketch, "E11", {"start": v(-85.48, 42.02) * mm, "mid": v(-95.25, 0) * mm, "end": v(-85.48, -42.02) * mm});
            skLineSegment(sketch, "E12.rect.left", {"start": v(6.35, 95.04) * mm, "end": v(6.35, 17.96) * mm});
            skLineSegment(sketch, "E12.rect.right", {"start": v(-6.35, 95.04) * mm, "end": v(-6.35, 17.96) * mm});
            skPoint(sketch, "E12.rect.top.end.orphan", {"position": v(-6.35, -100.16) * mm});
            skPoint(sketch, "E13.trimOffspring.end.orphan", {"position": v(6.35, -100.16) * mm});
            skPoint(sketch, "E14.orphan", {"position": v(6.35, 100.16) * mm});
            skPoint(sketch, "E15.orphan", {"position": v(-6.35, 100.16) * mm});
            skLineSegment(sketch, "E16.1.0", {"start": v(-85.48, 42.02) * mm, "end": v(-18.73, 3.48) * mm});
            skLineSegment(sketch, "E16.1.2", {"start": v(-79.13, 53.02) * mm, "end": v(-12.38, 14.48) * mm});
            skPoint(sketch, "E16.1.3", {"position": v(-89.92, 44.58) * mm});
            skPoint(sketch, "E16.1.4", {"position": v(-83.57, 55.58) * mm});
            skLineSegment(sketch, "E16.2.0", {"start": v(-79.13, -53.02) * mm, "end": v(-12.38, -14.48) * mm});
            skLineSegment(sketch, "E16.2.2", {"start": v(-85.48, -42.02) * mm, "end": v(-18.73, -3.48) * mm});
            skPoint(sketch, "E16.2.3", {"position": v(-83.57, -55.58) * mm});
            skPoint(sketch, "E16.2.4", {"position": v(-89.92, -44.58) * mm});
            skLineSegment(sketch, "E16.3.0", {"start": v(6.35, -95.04) * mm, "end": v(6.35, -17.96) * mm});
            skLineSegment(sketch, "E16.3.2", {"start": v(-6.35, -95.04) * mm, "end": v(-6.35, -17.96) * mm});
            skLineSegment(sketch, "E16.4.0", {"start": v(85.48, -42.02) * mm, "end": v(18.73, -3.48) * mm});
            skLineSegment(sketch, "E16.4.2", {"start": v(79.13, -53.02) * mm, "end": v(12.38, -14.48) * mm});
            skPoint(sketch, "E16.4.3", {"position": v(89.92, -44.58) * mm});
            skPoint(sketch, "E16.4.4", {"position": v(83.57, -55.58) * mm});
            skLineSegment(sketch, "E16.5.0", {"start": v(79.13, 53.02) * mm, "end": v(12.38, 14.48) * mm});
            skLineSegment(sketch, "E16.5.2", {"start": v(85.48, 42.02) * mm, "end": v(18.73, 3.48) * mm});
            skPoint(sketch, "E16.5.3", {"position": v(83.57, 55.58) * mm});
            skPoint(sketch, "E16.5.4", {"position": v(89.92, 44.58) * mm});
            skArc(sketch, "E17", {"start": v(-12.38, -14.48) * mm, "mid": v(-9.52, -16.5) * mm, "end": v(-6.35, -17.96) * mm});
            skArc(sketch, "E18.trimOffspring", {"start": v(-6.35, 95.04) * mm, "mid": v(-47.62, 82.49) * mm, "end": v(-79.13, 53.02) * mm});
            skArc(sketch, "E19.trimOffspring", {"start": v(79.13, 53.02) * mm, "mid": v(47.63, 82.49) * mm, "end": v(6.35, 95.04) * mm});
            skArc(sketch, "E20.trimOffspring", {"start": v(85.48, -42.02) * mm, "mid": v(95.25, 0) * mm, "end": v(85.48, 42.02) * mm});
            skArc(sketch, "E21.trimOffspring", {"start": v(6.35, -95.04) * mm, "mid": v(47.62, -82.49) * mm, "end": v(79.13, -53.02) * mm});
            skArc(sketch, "E22.trimOffspring", {"start": v(-79.13, -53.02) * mm, "mid": v(-47.63, -82.49) * mm, "end": v(-6.35, -95.04) * mm});
            skPoint(sketch, "E23.trimOffspring.end.orphan", {"position": v(-6.35, 0) * mm});
            skPoint(sketch, "E24.orphan", {"position": v(3.18, 5.5) * mm});
            skArc(sketch, "E25.trimOffspring", {"start": v(-18.73, 3.48) * mm, "mid": v(-19.05, 0) * mm, "end": v(-18.73, -3.48) * mm});
            skArc(sketch, "E26.trimOffspring", {"start": v(-6.35, 17.96) * mm, "mid": v(-9.52, 16.5) * mm, "end": v(-12.38, 14.48) * mm});
            skArc(sketch, "E27.trimOffspring", {"start": v(12.38, 14.48) * mm, "mid": v(9.53, 16.5) * mm, "end": v(6.35, 17.96) * mm});
            skPoint(sketch, "E28.orphan", {"position": v(6.35, 0) * mm});
            skArc(sketch, "E29.trimOffspring", {"start": v(6.35, -17.96) * mm, "mid": v(9.52, -16.5) * mm, "end": v(12.38, -14.48) * mm});
            skArc(sketch, "E30.trimOffspring", {"start": v(18.73, -3.48) * mm, "mid": v(19.05, 0) * mm, "end": v(18.73, 3.48) * mm});
            skSolve(sketch);
        }
        {
            var Q0;
            Q0 = qSketchRegion(id + "F7", true);
            extrude(context, id + "F8", {"entities" : qUnion([Q0]), "operationType" : NewBodyOperationType.REMOVE, "endBound" : BoundingType.THROUGH_ALL, "oppositeDirection" : true, "depth" : 25.4 * mm});
        }
        {
            var Q0;
            Q0=makeQuery(id+"F5.opExtrude","CAP_FACE",FACE,{"disambiguationData":[OSD([sQuery(id+"F4.wireOp",EDGE,"E10")])],"isStart":false});
            var sketch = newSketch(context, id + "F9", { "sketchPlane" : qUnion([Q0])});
            skCircle(sketch, "E31", {"center": v(0, 0) * mm, "radius": 6.35 * mm});
            skSolve(sketch);
        }
        {
            var Q0;
            Q0 = qSketchRegion(id + "F9", true);
            extrude(context, id + "F10", {"entities" : qUnion([Q0]), "operationType" : NewBodyOperationType.REMOVE, "endBound" : BoundingType.THROUGH_ALL, "oppositeDirection" : true, "depth" : 25.4 * mm});
        }
        {
            var Q0;
            Q0=makeQuery(id+"F5.opExtrude","SWEPT_BODY",BODY,{"disambiguationData":[OSD([sQuery(id+"F4.wireOp",EDGE,"E10")])]});
            deleteBodies(context, id + "F11", {"entities" : qUnion([Q0])});
        }
        {
            var Q0;
            Q0=qCreatedBy(makeId("Right.planeOp"),FACE);
            var sketch = newSketch(context, id + "F12", { "sketchPlane" : qUnion([Q0])});
            skLineSegment(sketch, "E32", {"start": v(-113.32, 3.36) * mm, "end": v(-113.32, 9.34) * mm});
            skLineSegment(sketch, "E33", {"start": v(-113.32, 9.34) * mm, "end": v(-101.6, 12.7) * mm});
            skLineSegment(sketch, "E34", {"start": v(-101.6, 0) * mm, "end": v(-113.32, 3.36) * mm});
            skLineSegment(sketch, "E35", {"start": v(-101.6, 0) * mm, "end": v(-101.6, 0) * mm});
            skLineSegment(sketch, "E36", {"start": v(-101.6, 0) * mm, "end": v(-119.44, 0) * mm});
            skLineSegment(sketch, "E37", {"start": v(-119.44, 0) * mm, "end": v(-119.44, 12.7) * mm});
            skLineSegment(sketch, "E38", {"start": v(-119.44, 12.7) * mm, "end": v(-101.6, 12.7) * mm});
            skLineSegment(sketch, "E39", {"start": v(0, 0) * mm, "end": v(0, -54.5) * mm, "construction": true});
            skSolve(sketch);
        }
        {
            var Q0;
            Q0 = qSketchRegion(id + "F12", true);
            var Q1;
            Q1=sQuery(id+"F12.wireOp",EDGE,"E39");
            revolve(context, id + "F13", {"operationType" : NewBodyOperationType.REMOVE, "entities" : qUnion([Q0]), "axis" : qUnion([Q1]), "revolveType" : RevolveType.FULL, "oppositeDirection" : true});
        }
    });
